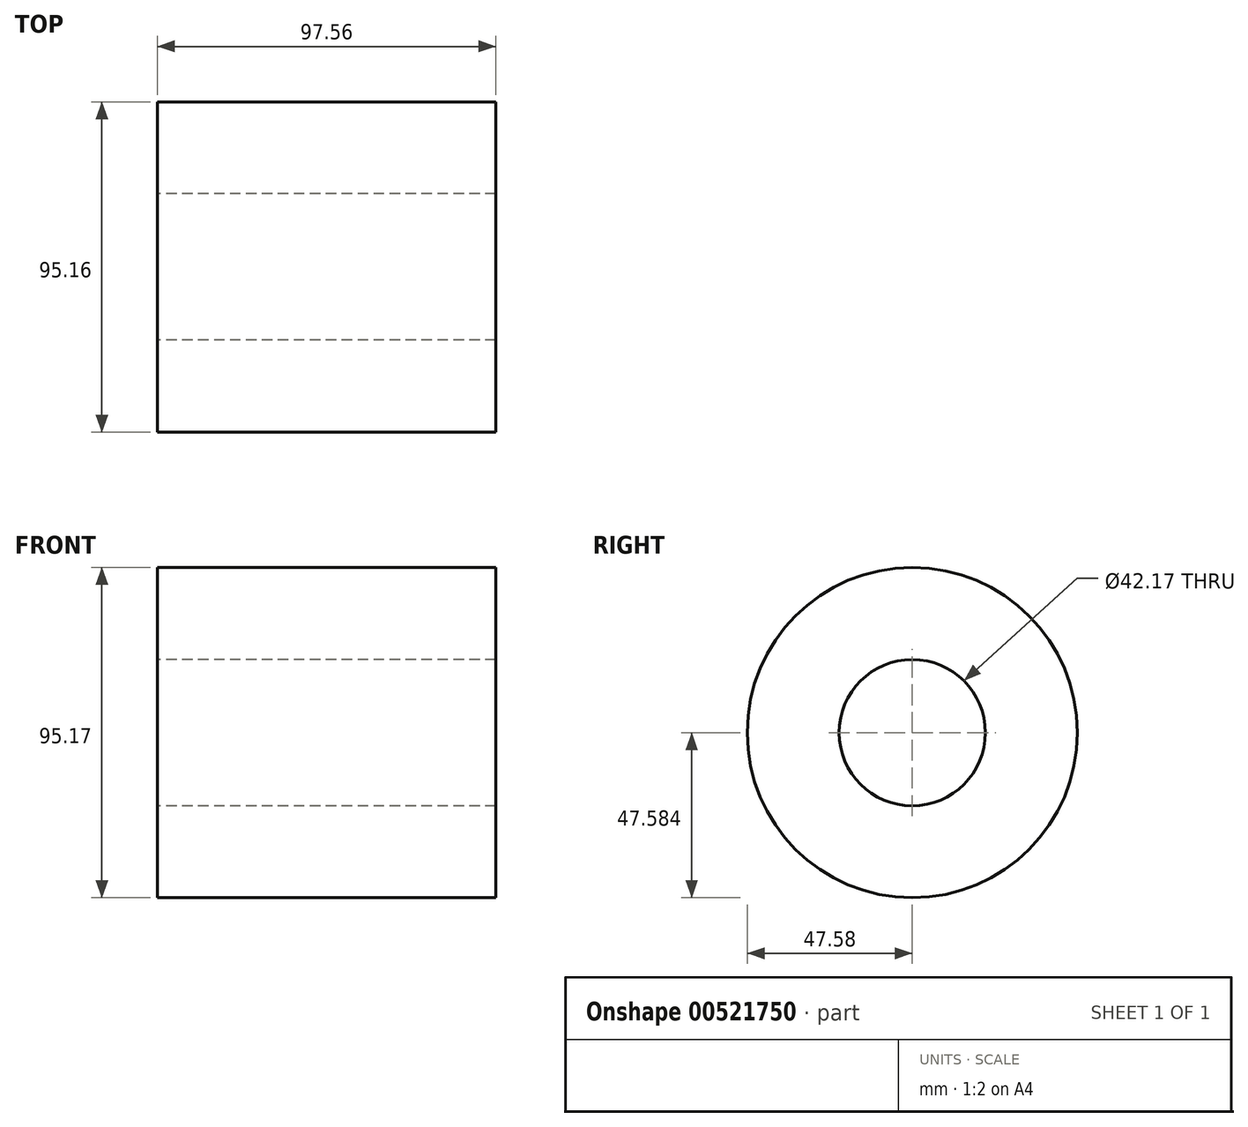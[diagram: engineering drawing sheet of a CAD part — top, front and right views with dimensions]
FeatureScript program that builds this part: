
annotation { "Feature Type Name" : "Feature", "Feature Type Description" : "" }
export const myFeature = defineFeature(function(context is Context, id is Id, definition is map)
    precondition{}
    {
        {
            var Q0;
            Q0=qCreatedBy(makeId("Front.planeOp"),FACE);
            var sketch = newSketch(context, id + "F0", { "sketchPlane" : qUnion([Q0])});
            skLineSegment(sketch, "E0.bottom", {"start": v(-47.34, 30.19) * mm, "end": v(50.22, 30.19) * mm});
            skLineSegment(sketch, "E0.top", {"start": v(-47.34, 56.69) * mm, "end": v(50.22, 56.69) * mm});
            skLineSegment(sketch, "E0.left", {"start": v(-47.34, 30.19) * mm, "end": v(-47.34, 56.69) * mm});
            skLineSegment(sketch, "E0.right", {"start": v(50.22, 30.19) * mm, "end": v(50.22, 56.69) * mm});
            skLineSegment(sketch, "E1", {"start": v(-52.74, 9.1) * mm, "end": v(58.24, 9.1) * mm});
            skSolve(sketch);
        }
        {
            var Q0;
            Q0 = qSketchRegion(id + "F0", true);
            var Q1;
            Q1=sQuery(id+"F0.wireOp",EDGE,"E1");
            revolve(context, id + "F1", {"entities" : qUnion([Q0]), "axis" : qUnion([Q1]), "revolveType" : RevolveType.FULL});
        }
    });
